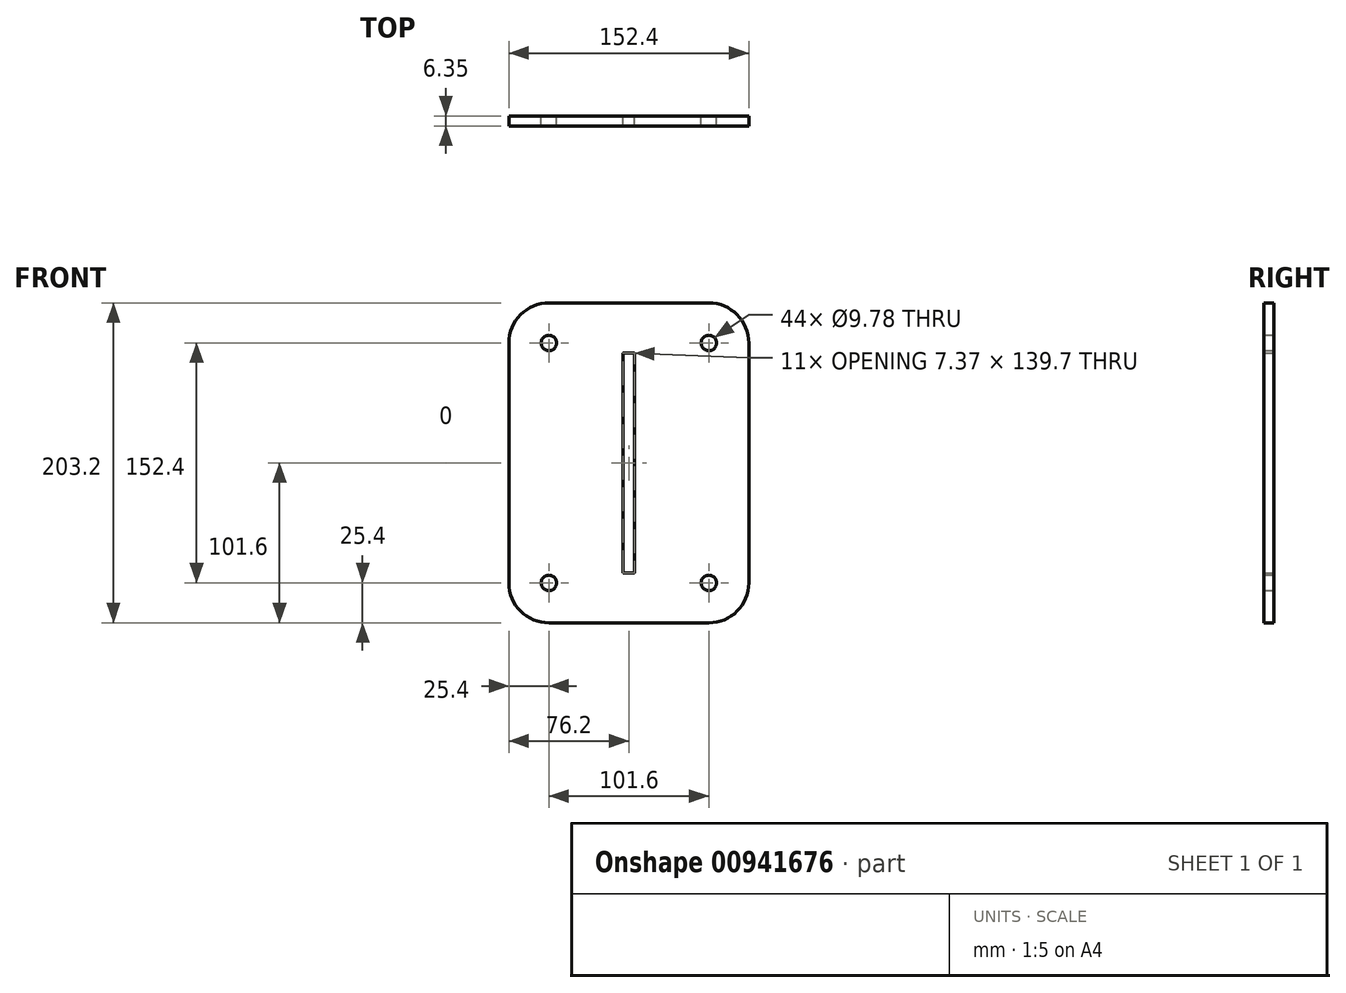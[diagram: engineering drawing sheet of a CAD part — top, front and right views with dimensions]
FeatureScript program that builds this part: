
annotation { "Feature Type Name" : "Feature", "Feature Type Description" : "" }
export const myFeature = defineFeature(function(context is Context, id is Id, definition is map)
    precondition{}
    {
        {
            var Q0;
            Q0=qCreatedBy(makeId("Front.planeOp"),FACE);
            var sketch = newSketch(context, id + "F0", { "sketchPlane" : qUnion([Q0])});
            skLineSegment(sketch, "E0.bottom", {"start": v(-50.8, -101.6) * mm, "end": v(50.8, -101.6) * mm});
            skLineSegment(sketch, "E0.top", {"start": v(-50.8, 101.6) * mm, "end": v(50.8, 101.6) * mm});
            skLineSegment(sketch, "E0.left", {"start": v(-76.2, -76.2) * mm, "end": v(-76.2, 76.2) * mm});
            skLineSegment(sketch, "E0.right", {"start": v(76.2, -76.2) * mm, "end": v(76.2, 76.2) * mm});
            skPoint(sketch, "E0.middle", {"position": v(0, 0) * mm});
            skCircle(sketch, "E1", {"center": v(-50.8, -76.2) * mm, "radius": 4.89 * mm});
            skCircle(sketch, "E2", {"center": v(-50.8, 76.2) * mm, "radius": 4.89 * mm});
            skCircle(sketch, "E3", {"center": v(50.8, 76.2) * mm, "radius": 4.89 * mm});
            skCircle(sketch, "E4", {"center": v(50.8, -76.2) * mm, "radius": 4.89 * mm});
            skLineSegment(sketch, "E5.bottom", {"start": v(-3.37, -69.85) * mm, "end": v(3.37, -69.85) * mm});
            skLineSegment(sketch, "E5.top", {"start": v(-3.37, 69.85) * mm, "end": v(3.37, 69.85) * mm});
            skLineSegment(sketch, "E5.left", {"start": v(-3.68, -69.53) * mm, "end": v(-3.68, 69.53) * mm});
            skLineSegment(sketch, "E5.right", {"start": v(3.68, -69.53) * mm, "end": v(3.68, 69.53) * mm});
            skPoint(sketch, "E6.visualSharp", {"position": v(-3.68, 69.85) * mm});
            skArc(sketch, "E6.filletArc", {"start": v(-3.37, 69.85) * mm, "mid": v(-3.6, 69.76) * mm, "end": v(-3.68, 69.53) * mm});
            skPoint(sketch, "E7.visualSharp", {"position": v(3.68, 69.85) * mm});
            skArc(sketch, "E7.filletArc", {"start": v(3.68, 69.53) * mm, "mid": v(3.6, 69.76) * mm, "end": v(3.37, 69.85) * mm});
            skPoint(sketch, "E8.visualSharp", {"position": v(3.68, -69.85) * mm});
            skArc(sketch, "E8.filletArc", {"start": v(3.37, -69.85) * mm, "mid": v(3.6, -69.76) * mm, "end": v(3.68, -69.53) * mm});
            skPoint(sketch, "E9.visualSharp", {"position": v(-3.68, -69.85) * mm});
            skArc(sketch, "E9.filletArc", {"start": v(-3.68, -69.53) * mm, "mid": v(-3.6, -69.76) * mm, "end": v(-3.37, -69.85) * mm});
            skPoint(sketch, "E10.visualSharp", {"position": v(-76.2, -101.6) * mm});
            skArc(sketch, "E10.filletArc", {"start": v(-76.2, -76.2) * mm, "mid": v(-68.76, -94.16) * mm, "end": v(-50.8, -101.6) * mm});
            skPoint(sketch, "E11.visualSharp", {"position": v(76.2, -101.6) * mm});
            skArc(sketch, "E11.filletArc", {"start": v(50.8, -101.6) * mm, "mid": v(68.76, -94.16) * mm, "end": v(76.2, -76.2) * mm});
            skPoint(sketch, "E12.visualSharp", {"position": v(76.2, 101.6) * mm});
            skArc(sketch, "E12.filletArc", {"start": v(76.2, 76.2) * mm, "mid": v(68.76, 94.16) * mm, "end": v(50.8, 101.6) * mm});
            skPoint(sketch, "E13.visualSharp", {"position": v(-76.2, 101.6) * mm});
            skArc(sketch, "E13.filletArc", {"start": v(-50.8, 101.6) * mm, "mid": v(-68.76, 94.16) * mm, "end": v(-76.2, 76.2) * mm});
            skSolve(sketch);
        }
        {
            var Q0;
            Q0=makeQuery(id+"F0.imprint","IMPRINT",FACE,{"disambiguationData":[TD([[makeQuery(id+"F0.imprint","IMPRINT",EDGE,{"derivedFrom":sQuery(id+"F0.wireOp",EDGE,"E0.bottom")}),1.0]])]});
            extrude(context, id + "F1", {"entities" : qUnion([Q0]), "depth" : 6.35 * mm, "offsetDistance" : 25.4 * mm});
        }
    });
